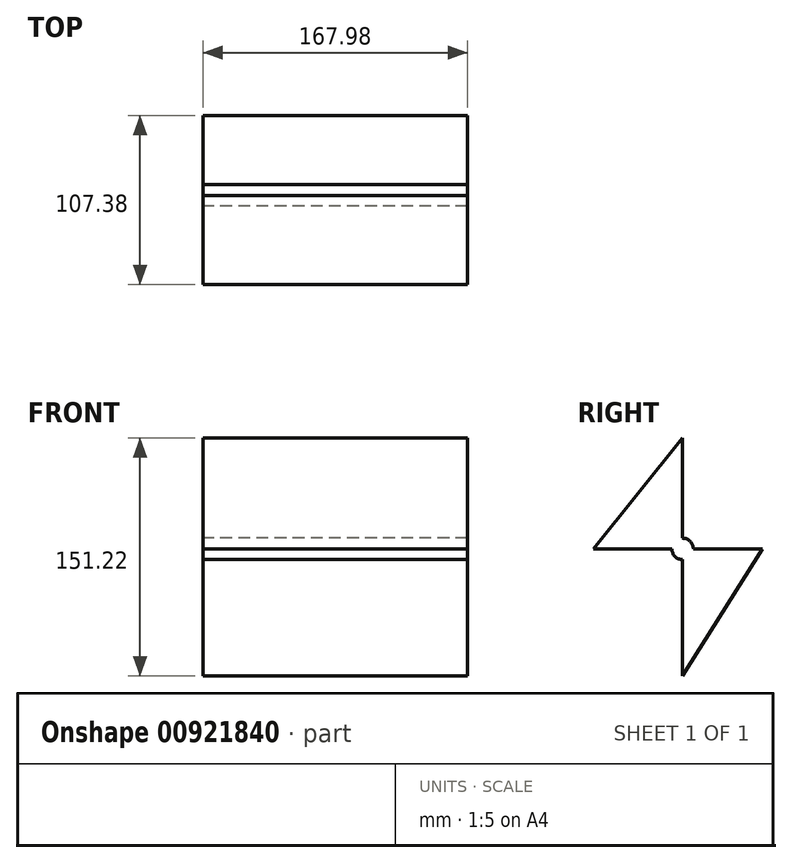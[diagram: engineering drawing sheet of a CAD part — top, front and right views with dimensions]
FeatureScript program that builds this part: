
annotation { "Feature Type Name" : "Feature", "Feature Type Description" : "" }
export const myFeature = defineFeature(function(context is Context, id is Id, definition is map)
    precondition{}
    {
        {
            var Q0;
            Q0=qCreatedBy(makeId("Right.planeOp"),FACE);
            var sketch = newSketch(context, id + "F0", { "sketchPlane" : qUnion([Q0])});
            skLineSegment(sketch, "E0", {"start": v(-56.65, 0) * mm, "end": v(0, 70.46) * mm});
            skLineSegment(sketch, "E1", {"start": v(0, 70.46) * mm, "end": v(0, 16.55) * mm});
            skLineSegment(sketch, "E2", {"start": v(0, 16.55) * mm, "end": v(0, 6.82) * mm});
            skLineSegment(sketch, "E3", {"start": v(50.73, 0) * mm, "end": v(6.82, 0) * mm});
            skArc(sketch, "E4", {"start": v(-6.82, 0) * mm, "mid": v(-4.82, -4.82) * mm, "end": v(0, -6.82) * mm});
            skLineSegment(sketch, "E5.trimOffspring", {"start": v(-6.82, 0) * mm, "end": v(-56.65, 0) * mm});
            skArc(sketch, "E6.trimOffspring", {"start": v(6.82, 0) * mm, "mid": v(4.82, 4.82) * mm, "end": v(0, 6.82) * mm});
            skLineSegment(sketch, "E7", {"start": v(50.73, 0) * mm, "end": v(0, -80.76) * mm});
            skLineSegment(sketch, "E8", {"start": v(0, -80.76) * mm, "end": v(0, -6.82) * mm});
            skPoint(sketch, "E9.trimOffspring.end.orphan", {"position": v(0, -49.4) * mm});
            skSolve(sketch);
        }
        {
            var Q0;
            Q0=qCreatedBy(makeId("Front.planeOp"),FACE);
            var sketch = newSketch(context, id + "F1", { "sketchPlane" : qUnion([Q0])});
            skLineSegment(sketch, "E10", {"start": v(0, 0) * mm, "end": v(0, 70.2) * mm});
            skLineSegment(sketch, "E11", {"start": v(0, 70.2) * mm, "end": v(39.99, 60.18) * mm});
            skLineSegment(sketch, "E12", {"start": v(40.41, 47.99) * mm, "end": v(39.31, 47.63) * mm});
            skLineSegment(sketch, "E13", {"start": v(38.71, 35.79) * mm, "end": v(53.92, 29.05) * mm});
            skLineSegment(sketch, "E14", {"start": v(53.3, 17.2) * mm, "end": v(13.68, 4.41) * mm});
            skLineSegment(sketch, "E15.MirrorCS", {"start": v(53.3, -17.2) * mm, "end": v(13.68, -4.41) * mm});
            skLineSegment(sketch, "E16.MirrorCS", {"start": v(40.41, -47.99) * mm, "end": v(39.31, -47.63) * mm});
            skLineSegment(sketch, "E17.MirrorCS", {"start": v(38.71, -35.79) * mm, "end": v(53.92, -29.05) * mm});
            skLineSegment(sketch, "E18.MirrorCS", {"start": v(0, -70.2) * mm, "end": v(39.99, -60.18) * mm});
            skLineSegment(sketch, "E19", {"start": v(0, 70.2) * mm, "end": v(0, -70.2) * mm});
            skPoint(sketch, "E20.orphan", {"position": v(0, 0) * mm});
            skPoint(sketch, "E21.visualSharp", {"position": v(61.36, 54.83) * mm});
            skArc(sketch, "E21.filletArc", {"start": v(40.41, 47.99) * mm, "mid": v(44.79, 54.25) * mm, "end": v(39.99, 60.18) * mm});
            skPoint(sketch, "E22.visualSharp", {"position": v(23.58, 42.5) * mm});
            skArc(sketch, "E22.filletArc", {"start": v(39.31, 47.63) * mm, "mid": v(34.94, 41.91) * mm, "end": v(38.71, 35.79) * mm});
            skPoint(sketch, "E23.visualSharp", {"position": v(69.13, 22.3) * mm});
            skArc(sketch, "E23.filletArc", {"start": v(53.3, 17.2) * mm, "mid": v(57.69, 22.9) * mm, "end": v(53.92, 29.05) * mm});
            skPoint(sketch, "E24.visualSharp", {"position": v(69.13, -22.3) * mm});
            skArc(sketch, "E24.filletArc", {"start": v(53.92, -29.05) * mm, "mid": v(57.69, -22.9) * mm, "end": v(53.3, -17.2) * mm});
            skPoint(sketch, "E25.visualSharp", {"position": v(61.36, -54.83) * mm});
            skArc(sketch, "E25.filletArc", {"start": v(39.99, -60.18) * mm, "mid": v(44.79, -54.25) * mm, "end": v(40.41, -47.99) * mm});
            skPoint(sketch, "E26.visualSharp", {"position": v(8.91, 2.88) * mm});
            skArc(sketch, "E26.filletArc", {"start": v(7.98, 5.33) * mm, "mid": v(10.72, 4.19) * mm, "end": v(13.68, 4.41) * mm});
            skPoint(sketch, "E27.visualSharp", {"position": v(8.91, -2.88) * mm});
            skArc(sketch, "E27.filletArc", {"start": v(13.68, -4.41) * mm, "mid": v(10.72, -4.19) * mm, "end": v(7.98, -5.33) * mm});
            skArc(sketch, "E28", {"start": v(5.77, 5.07) * mm, "mid": v(3.92, 0) * mm, "end": v(5.77, -5.07) * mm});
            skPoint(sketch, "E29.visualSharp", {"position": v(7, -6.23) * mm});
            skArc(sketch, "E29.filletArc", {"start": v(5.77, -5.07) * mm, "mid": v(6.82, -5.64) * mm, "end": v(7.98, -5.33) * mm});
            skPoint(sketch, "E30.visualSharp", {"position": v(7, 6.23) * mm});
            skArc(sketch, "E30.filletArc", {"start": v(7.98, 5.33) * mm, "mid": v(6.82, 5.64) * mm, "end": v(5.77, 5.07) * mm});
            skPoint(sketch, "E31.visualSharp", {"position": v(23.58, -42.5) * mm});
            skArc(sketch, "E31.filletArc", {"start": v(38.71, -35.79) * mm, "mid": v(34.94, -41.91) * mm, "end": v(39.31, -47.63) * mm});
            skSolve(sketch);
        }
        {
            var Q0;
            Q0=makeQuery(id+"F0.imprint","IMPRINT",FACE,{"disambiguationData":[TD([[makeQuery(id+"F0.imprint","IMPRINT",EDGE,{"derivedFrom":sQuery(id+"F0.wireOp",EDGE,"E0")}),-1.0]])]});
            extrude(context, id + "F2", {"entities" : qUnion([Q0]), "depth" : 115.18 * mm, "offsetDistance" : 25.4 * mm, "hasSecondDirection" : true, "secondDirectionOppositeDirection" : true, "secondDirectionDepth" : 52.8 * mm});
        }
        {
            var Q0;
            {var subQ1=sQuery(id+"F1.wireOp",EDGE,"E11");Q0=makeQuery(id+"F1.imprint","IMPRINT",FACE,{"disambiguationData":[TD([[makeQuery(id+"F1.imprint","IMPRINT",EDGE,{"derivedFrom":subQ1}),-1.0]])]});}
            var Q1;
            Q1=sQuery(id+"F1.wireOp",EDGE,"E18.MirrorCS");
            var Q2;
            Q2=sQuery(id+"F1.wireOp",EDGE,"E25.filletArc");
            var Q3;
            Q3=sQuery(id+"F1.wireOp",EDGE,"E31.filletArc");
            var Q4;
            Q4=sQuery(id+"F1.wireOp",EDGE,"E17.MirrorCS");
            var Q5;
            Q5=sQuery(id+"F1.wireOp",EDGE,"E15.MirrorCS");
            var Q6;
            Q6=sQuery(id+"F1.wireOp",EDGE,"E24.filletArc");
            var Q7;
            Q7=sQuery(id+"F1.wireOp",EDGE,"E27.filletArc");
            var Q8;
            Q8=sQuery(id+"F1.wireOp",EDGE,"E28");
            var Q9;
            Q9=sQuery(id+"F1.wireOp",EDGE,"E29.filletArc");
            var Q10;
            Q10=sQuery(id+"F1.wireOp",EDGE,"E30.filletArc");
            var Q11;
            Q11=sQuery(id+"F1.wireOp",EDGE,"E26.filletArc");
            var Q12;
            Q12=sQuery(id+"F1.wireOp",EDGE,"E14");
            var Q13;
            Q13=sQuery(id+"F1.wireOp",EDGE,"E23.filletArc");
            var Q14;
            Q14=sQuery(id+"F1.wireOp",EDGE,"E13");
            var Q15;
            Q15=sQuery(id+"F1.wireOp",EDGE,"E22.filletArc");
            var Q16;
            Q16=sQuery(id+"F1.wireOp",EDGE,"E21.filletArc");
            var Q17;
            Q17=sQuery(id+"F1.wireOp",EDGE,"E11");
            var Q18;
            Q18=sQuery(id+"F1.wireOp",EDGE,"E19");
            extrude(context, id + "F3", {"entities" : qUnion([Q0]), "bodyType" : ToolBodyType.SURFACE, "surfaceEntities" : qUnion([Q1, Q2, Q3, Q4, Q5, Q6, Q7, Q8, Q9, Q10, Q11, Q12, Q13, Q14, Q15, Q16, Q17, Q18]), "depth" : 91.3 * mm, "offsetDistance" : 25.4 * mm, "hasSecondDirection" : true, "secondDirectionOppositeDirection" : true, "secondDirectionDepth" : 106.17 * mm});
        }
    });
